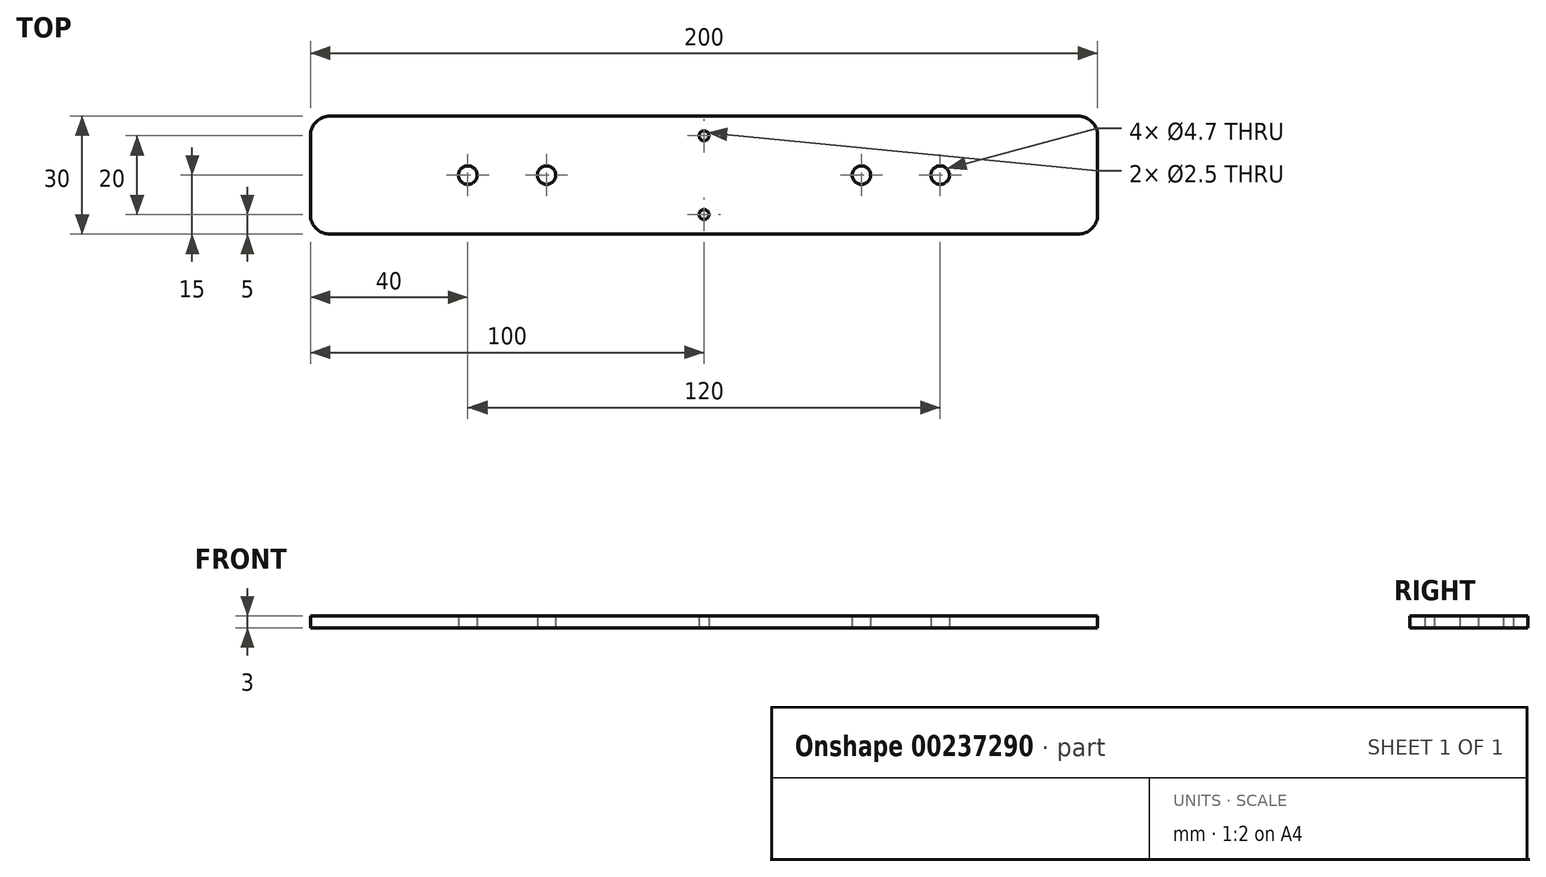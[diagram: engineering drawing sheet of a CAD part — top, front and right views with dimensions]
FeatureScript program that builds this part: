
annotation { "Feature Type Name" : "Feature", "Feature Type Description" : "" }
export const myFeature = defineFeature(function(context is Context, id is Id, definition is map)
    precondition{}
    {
        {
            var Q0;
            Q0=qCreatedBy(makeId("Top.planeOp"),FACE);
            var sketch = newSketch(context, id + "F0", { "sketchPlane" : qUnion([Q0])});
            skLineSegment(sketch, "E0.bottom", {"start": v(95, -15) * mm, "end": v(-95, -15) * mm});
            skLineSegment(sketch, "E0.top", {"start": v(95, 15) * mm, "end": v(-95, 15) * mm});
            skLineSegment(sketch, "E0.left", {"start": v(100, -10) * mm, "end": v(100, 10) * mm});
            skLineSegment(sketch, "E0.right", {"start": v(-100, -10) * mm, "end": v(-100, 10) * mm});
            skPoint(sketch, "E0.middle", {"position": v(0, 0) * mm});
            skPoint(sketch, "E1.visualSharp", {"position": v(-100, 15) * mm});
            skArc(sketch, "E1.filletArc", {"start": v(-95, 15) * mm, "mid": v(-98.54, 13.54) * mm, "end": v(-100, 10) * mm});
            skPoint(sketch, "E2.visualSharp", {"position": v(-100, -15) * mm});
            skArc(sketch, "E2.filletArc", {"start": v(-100, -10) * mm, "mid": v(-98.54, -13.54) * mm, "end": v(-95, -15) * mm});
            skPoint(sketch, "E3.visualSharp", {"position": v(100, 15) * mm});
            skArc(sketch, "E3.filletArc", {"start": v(100, 10) * mm, "mid": v(98.54, 13.54) * mm, "end": v(95, 15) * mm});
            skPoint(sketch, "E4.visualSharp", {"position": v(100, -15) * mm});
            skArc(sketch, "E4.filletArc", {"start": v(95, -15) * mm, "mid": v(98.54, -13.54) * mm, "end": v(100, -10) * mm});
            skCircle(sketch, "E5", {"center": v(60, 0) * mm, "radius": 2.35 * mm});
            skCircle(sketch, "E6", {"center": v(40, 0) * mm, "radius": 2.35 * mm});
            skCircle(sketch, "E7", {"center": v(-60, 0) * mm, "radius": 2.35 * mm});
            skCircle(sketch, "E8", {"center": v(-40, 0) * mm, "radius": 2.35 * mm});
            skCircle(sketch, "E9", {"center": v(0, 10) * mm, "radius": 1.25 * mm});
            skCircle(sketch, "E10", {"center": v(0, -10) * mm, "radius": 1.25 * mm});
            skSolve(sketch);
        }
        {
            var Q0;
            Q0=makeQuery(id+"F0.imprint","IMPRINT",FACE,{"disambiguationData":[TD([[makeQuery(id+"F0.imprint","IMPRINT",EDGE,{"derivedFrom":sQuery(id+"F0.wireOp",EDGE,"E0.bottom")}),-1.0]])]});
            extrude(context, id + "F1", {"entities" : qUnion([Q0]), "depth" : 3 * mm});
        }
    });
